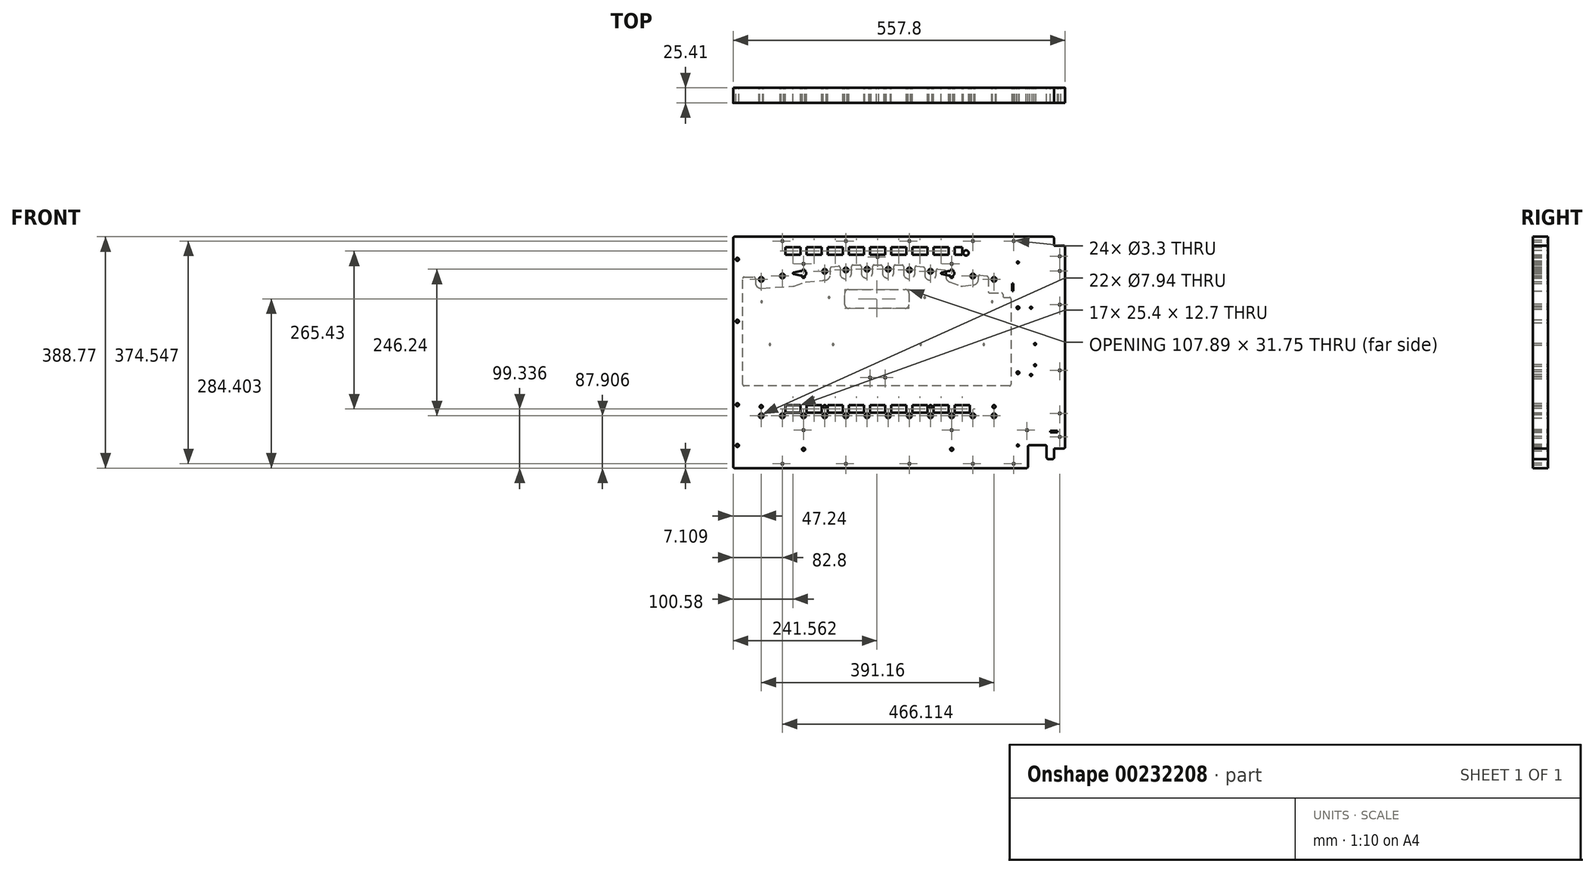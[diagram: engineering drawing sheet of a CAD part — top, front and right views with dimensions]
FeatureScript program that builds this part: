
annotation { "Feature Type Name" : "Feature", "Feature Type Description" : "" }
export const myFeature = defineFeature(function(context is Context, id is Id, definition is map)
    precondition{}
    {
        {
            var Q0;
            Q0=qCreatedBy(makeId("Front.planeOp"),FACE);
            var sketch = newSketch(context, id + "F0", { "sketchPlane" : qUnion([Q0])});
            skCircle(sketch, "E0", {"center": v(270.01, 168.97) * mm, "radius": 1.65 * mm});
            skCircle(sketch, "E1", {"center": v(270.01, 144.35) * mm, "radius": 1.65 * mm});
            skCircle(sketch, "E2", {"center": v(270.01, 87.69) * mm, "radius": 1.65 * mm});
            skCircle(sketch, "E3", {"center": v(270.01, -22.8) * mm, "radius": 1.65 * mm});
            skCircle(sketch, "E4", {"center": v(270.01, -134.56) * mm, "radius": 1.65 * mm});
            skCircle(sketch, "E5", {"center": v(270.01, -95.2) * mm, "radius": 1.65 * mm});
            skCircle(sketch, "E6", {"center": v(-196.1, -179.8) * mm, "radius": 1.65 * mm});
            skCircle(sketch, "E7", {"center": v(-89.42, -179.8) * mm, "radius": 1.65 * mm});
            skCircle(sketch, "E8", {"center": v(17.26, -179.8) * mm, "radius": 1.65 * mm});
            skCircle(sketch, "E9", {"center": v(123.94, -179.8) * mm, "radius": 1.65 * mm});
            skCircle(sketch, "E10", {"center": v(192.52, -179.8) * mm, "radius": 1.65 * mm});
            skCircle(sketch, "E11", {"center": v(-196.1, 194.75) * mm, "radius": 1.65 * mm});
            skCircle(sketch, "E12", {"center": v(-89.42, 194.75) * mm, "radius": 1.65 * mm});
            skCircle(sketch, "E13", {"center": v(17.26, 194.75) * mm, "radius": 1.65 * mm});
            skCircle(sketch, "E14", {"center": v(123.94, 194.75) * mm, "radius": 1.65 * mm});
            skCircle(sketch, "E15", {"center": v(192.52, 194.75) * mm, "radius": 1.65 * mm});
            skCircle(sketch, "E16", {"center": v(-196.1, 136) * mm, "radius": 3.97 * mm});
            skCircle(sketch, "E17", {"center": v(-124.98, 143.87) * mm, "radius": 3.97 * mm});
            skCircle(sketch, "E18", {"center": v(-89.42, 146.12) * mm, "radius": 3.97 * mm});
            skCircle(sketch, "E19", {"center": v(-53.86, 147.24) * mm, "radius": 3.97 * mm});
            skCircle(sketch, "E20", {"center": v(17.26, 146.12) * mm, "radius": 3.97 * mm});
            skCircle(sketch, "E21", {"center": v(-18.3, 147.24) * mm, "radius": 3.97 * mm});
            skCircle(sketch, "E22", {"center": v(52.82, 143.87) * mm, "radius": 3.97 * mm});
            skCircle(sketch, "E23", {"center": v(123.94, 136) * mm, "radius": 3.97 * mm});
            skCircle(sketch, "E24", {"center": v(-196.1, -99) * mm, "radius": 3.97 * mm});
            skCircle(sketch, "E25", {"center": v(-160.54, -99) * mm, "radius": 3.97 * mm});
            skCircle(sketch, "E26", {"center": v(-124.98, -99) * mm, "radius": 3.97 * mm});
            skCircle(sketch, "E27", {"center": v(-89.42, -99) * mm, "radius": 3.97 * mm});
            skCircle(sketch, "E28", {"center": v(-53.86, -99) * mm, "radius": 3.97 * mm});
            skCircle(sketch, "E29", {"center": v(-18.3, -99) * mm, "radius": 3.97 * mm});
            skCircle(sketch, "E30", {"center": v(17.26, -99) * mm, "radius": 3.97 * mm});
            skCircle(sketch, "E31", {"center": v(52.82, -99) * mm, "radius": 3.97 * mm});
            skCircle(sketch, "E32", {"center": v(88.38, -99) * mm, "radius": 3.97 * mm});
            skCircle(sketch, "E33", {"center": v(123.94, -99) * mm, "radius": 3.97 * mm});
            skCircle(sketch, "E34", {"center": v(159.5, 130.33) * mm, "radius": 3.97 * mm});
            skCircle(sketch, "E35", {"center": v(159.5, -99) * mm, "radius": 3.97 * mm});
            skCircle(sketch, "E36", {"center": v(-231.66, -99) * mm, "radius": 3.97 * mm});
            skCircle(sketch, "E37", {"center": v(-231.66, 130.33) * mm, "radius": 3.97 * mm});
            skCircle(sketch, "E38", {"center": v(-271.8, 163.89) * mm, "radius": 2.54 * mm});
            skCircle(sketch, "E39", {"center": v(-271.8, 59.75) * mm, "radius": 2.54 * mm});
            skCircle(sketch, "E40", {"center": v(-271.8, -148.94) * mm, "radius": 2.54 * mm});
            skCircle(sketch, "E41", {"center": v(-160.54, 156.27) * mm, "radius": 1.65 * mm});
            skCircle(sketch, "E42", {"center": v(88.38, 156.27) * mm, "radius": 1.65 * mm});
            skCircle(sketch, "E43", {"center": v(-36.08, 167.95) * mm, "radius": 1.65 * mm});
            skCircle(sketch, "E44", {"center": v(199.63, 82.6) * mm, "radius": 2.29 * mm});
            skCircle(sketch, "E45", {"center": v(221.73, 82.6) * mm, "radius": 1.66 * mm});
            skCircle(sketch, "E46", {"center": v(199.63, -26.61) * mm, "radius": 2.29 * mm});
            skCircle(sketch, "E47", {"center": v(221.73, -30.42) * mm, "radius": 1.66 * mm});
            skCircle(sketch, "E48", {"center": v(-160.54, -155.3) * mm, "radius": 2.54 * mm});
            skCircle(sketch, "E49", {"center": v(88.38, -155.3) * mm, "radius": 2.54 * mm});
            skCircle(sketch, "E50", {"center": v(-231.66, -83.76) * mm, "radius": 2.54 * mm});
            skCircle(sketch, "E51", {"center": v(159.5, -83.76) * mm, "radius": 2.54 * mm});
            skCircle(sketch, "E52", {"center": v(-160.54, -123.13) * mm, "radius": 1.65 * mm});
            skCircle(sketch, "E53", {"center": v(88.38, -123.13) * mm, "radius": 1.65 * mm});
            skCircle(sketch, "E54", {"center": v(-271.8, -80.36) * mm, "radius": 2.54 * mm});
            skCircle(sketch, "E55", {"center": v(-124.98, -83.76) * mm, "radius": 2.54 * mm});
            skCircle(sketch, "E56", {"center": v(52.82, -83.76) * mm, "radius": 2.54 * mm});
            skCircle(sketch, "E57", {"center": v(228.49, -13.91) * mm, "radius": 1.66 * mm});
            skCircle(sketch, "E58", {"center": v(228.49, 21.65) * mm, "radius": 1.66 * mm});
            skCircle(sketch, "E59", {"center": v(112.5, 174.6) * mm, "radius": 4.45 * mm});
            skCircle(sketch, "E60", {"center": v(199.63, 158.8) * mm, "radius": 1.66 * mm});
            skCircle(sketch, "E61", {"center": v(199.63, -148.94) * mm, "radius": 1.66 * mm});
            skCircle(sketch, "E62", {"center": v(-48.78, -34.87) * mm, "radius": 1.65 * mm});
            skCircle(sketch, "E63", {"center": v(-23.38, -34.87) * mm, "radius": 1.65 * mm});
            skCircle(sketch, "E64", {"center": v(214.97, -123.13) * mm, "radius": 1.65 * mm});
            skLineSegment(sketch, "E65", {"start": v(-48.78, 171.5) * mm, "end": v(-23.38, 171.5) * mm});
            skLineSegment(sketch, "E66", {"start": v(-23.38, 171.5) * mm, "end": v(-23.38, 184.2) * mm});
            skLineSegment(sketch, "E67", {"start": v(-23.38, 184.2) * mm, "end": v(-48.78, 184.2) * mm});
            skLineSegment(sketch, "E68", {"start": v(-48.78, 184.2) * mm, "end": v(-48.78, 171.5) * mm});
            skLineSegment(sketch, "E69", {"start": v(-58.94, 184.2) * mm, "end": v(-84.34, 184.2) * mm});
            skLineSegment(sketch, "E70", {"start": v(-84.34, 184.2) * mm, "end": v(-84.34, 171.5) * mm});
            skLineSegment(sketch, "E71", {"start": v(-84.34, 171.5) * mm, "end": v(-58.94, 171.5) * mm});
            skLineSegment(sketch, "E72", {"start": v(-58.94, 171.5) * mm, "end": v(-58.94, 184.2) * mm});
            skLineSegment(sketch, "E73", {"start": v(-94.5, 184.2) * mm, "end": v(-119.9, 184.2) * mm});
            skLineSegment(sketch, "E74", {"start": v(-119.9, 184.2) * mm, "end": v(-119.9, 171.5) * mm});
            skLineSegment(sketch, "E75", {"start": v(-119.9, 171.5) * mm, "end": v(-94.5, 171.5) * mm});
            skLineSegment(sketch, "E76", {"start": v(-94.5, 171.5) * mm, "end": v(-94.5, 184.2) * mm});
            skLineSegment(sketch, "E77", {"start": v(-130.06, 184.2) * mm, "end": v(-155.46, 184.2) * mm});
            skLineSegment(sketch, "E78", {"start": v(-155.46, 184.2) * mm, "end": v(-155.46, 171.5) * mm});
            skLineSegment(sketch, "E79", {"start": v(-155.46, 171.5) * mm, "end": v(-130.06, 171.5) * mm});
            skLineSegment(sketch, "E80", {"start": v(-130.06, 171.5) * mm, "end": v(-130.06, 184.2) * mm});
            skLineSegment(sketch, "E81", {"start": v(-165.62, 184.2) * mm, "end": v(-191.02, 184.2) * mm});
            skLineSegment(sketch, "E82", {"start": v(-191.02, 184.2) * mm, "end": v(-191.02, 171.5) * mm});
            skLineSegment(sketch, "E83", {"start": v(-191.02, 171.5) * mm, "end": v(-165.62, 171.5) * mm});
            skLineSegment(sketch, "E84", {"start": v(-165.62, 171.5) * mm, "end": v(-165.62, 184.2) * mm});
            skLineSegment(sketch, "E85", {"start": v(-13.22, 171.5) * mm, "end": v(12.18, 171.5) * mm});
            skLineSegment(sketch, "E86", {"start": v(12.18, 171.5) * mm, "end": v(12.18, 184.2) * mm});
            skLineSegment(sketch, "E87", {"start": v(12.18, 184.2) * mm, "end": v(-13.22, 184.2) * mm});
            skLineSegment(sketch, "E88", {"start": v(-13.22, 184.2) * mm, "end": v(-13.22, 171.5) * mm});
            skLineSegment(sketch, "E89", {"start": v(22.34, 171.5) * mm, "end": v(47.74, 171.5) * mm});
            skLineSegment(sketch, "E90", {"start": v(47.74, 171.5) * mm, "end": v(47.74, 184.2) * mm});
            skLineSegment(sketch, "E91", {"start": v(47.74, 184.2) * mm, "end": v(22.34, 184.2) * mm});
            skLineSegment(sketch, "E92", {"start": v(22.34, 184.2) * mm, "end": v(22.34, 171.5) * mm});
            skLineSegment(sketch, "E93", {"start": v(57.9, 171.5) * mm, "end": v(83.3, 171.5) * mm});
            skLineSegment(sketch, "E94", {"start": v(83.3, 171.5) * mm, "end": v(83.3, 184.2) * mm});
            skLineSegment(sketch, "E95", {"start": v(83.3, 184.2) * mm, "end": v(57.9, 184.2) * mm});
            skLineSegment(sketch, "E96", {"start": v(57.9, 184.2) * mm, "end": v(57.9, 171.5) * mm});
            skLineSegment(sketch, "E97", {"start": v(93.46, 171.5) * mm, "end": v(106.16, 171.5) * mm});
            skLineSegment(sketch, "E98", {"start": v(106.16, 171.5) * mm, "end": v(106.16, 184.2) * mm});
            skLineSegment(sketch, "E99", {"start": v(106.16, 184.2) * mm, "end": v(93.46, 184.2) * mm});
            skLineSegment(sketch, "E100", {"start": v(93.46, 184.2) * mm, "end": v(93.46, 171.5) * mm});
            skLineSegment(sketch, "E101", {"start": v(-48.78, -93.92) * mm, "end": v(-23.38, -93.92) * mm});
            skLineSegment(sketch, "E102", {"start": v(-23.38, -93.92) * mm, "end": v(-23.38, -81.22) * mm});
            skLineSegment(sketch, "E103", {"start": v(-23.38, -81.22) * mm, "end": v(-48.78, -81.22) * mm});
            skLineSegment(sketch, "E104", {"start": v(-48.78, -81.22) * mm, "end": v(-48.78, -93.92) * mm});
            skLineSegment(sketch, "E105", {"start": v(-58.94, -81.22) * mm, "end": v(-84.34, -81.22) * mm});
            skLineSegment(sketch, "E106", {"start": v(-84.34, -81.22) * mm, "end": v(-84.34, -93.92) * mm});
            skLineSegment(sketch, "E107", {"start": v(-84.34, -93.92) * mm, "end": v(-58.94, -93.92) * mm});
            skLineSegment(sketch, "E108", {"start": v(-58.94, -93.92) * mm, "end": v(-58.94, -81.22) * mm});
            skLineSegment(sketch, "E109", {"start": v(-94.5, -81.22) * mm, "end": v(-119.9, -81.22) * mm});
            skLineSegment(sketch, "E110", {"start": v(-119.9, -81.22) * mm, "end": v(-119.9, -93.92) * mm});
            skLineSegment(sketch, "E111", {"start": v(-119.9, -93.92) * mm, "end": v(-94.5, -93.92) * mm});
            skLineSegment(sketch, "E112", {"start": v(-94.5, -93.92) * mm, "end": v(-94.5, -81.22) * mm});
            skLineSegment(sketch, "E113", {"start": v(-130.06, -81.22) * mm, "end": v(-155.46, -81.22) * mm});
            skLineSegment(sketch, "E114", {"start": v(-155.46, -81.22) * mm, "end": v(-155.46, -93.92) * mm});
            skLineSegment(sketch, "E115", {"start": v(-155.46, -93.92) * mm, "end": v(-130.06, -93.92) * mm});
            skLineSegment(sketch, "E116", {"start": v(-130.06, -93.92) * mm, "end": v(-130.06, -81.22) * mm});
            skLineSegment(sketch, "E117", {"start": v(-165.62, -81.22) * mm, "end": v(-191.02, -81.22) * mm});
            skLineSegment(sketch, "E118", {"start": v(-191.02, -81.22) * mm, "end": v(-191.02, -93.92) * mm});
            skLineSegment(sketch, "E119", {"start": v(-191.02, -93.92) * mm, "end": v(-165.62, -93.92) * mm});
            skLineSegment(sketch, "E120", {"start": v(-165.62, -93.92) * mm, "end": v(-165.62, -81.22) * mm});
            skLineSegment(sketch, "E121", {"start": v(-13.22, -93.92) * mm, "end": v(12.18, -93.92) * mm});
            skLineSegment(sketch, "E122", {"start": v(12.18, -93.92) * mm, "end": v(12.18, -81.22) * mm});
            skLineSegment(sketch, "E123", {"start": v(12.18, -81.22) * mm, "end": v(-13.22, -81.22) * mm});
            skLineSegment(sketch, "E124", {"start": v(-13.22, -81.22) * mm, "end": v(-13.22, -93.92) * mm});
            skLineSegment(sketch, "E125", {"start": v(22.34, -93.92) * mm, "end": v(47.74, -93.92) * mm});
            skLineSegment(sketch, "E126", {"start": v(47.74, -93.92) * mm, "end": v(47.74, -81.22) * mm});
            skLineSegment(sketch, "E127", {"start": v(47.74, -81.22) * mm, "end": v(22.34, -81.22) * mm});
            skLineSegment(sketch, "E128", {"start": v(22.34, -81.22) * mm, "end": v(22.34, -93.92) * mm});
            skLineSegment(sketch, "E129", {"start": v(57.9, -93.92) * mm, "end": v(83.3, -93.92) * mm});
            skLineSegment(sketch, "E130", {"start": v(83.3, -93.92) * mm, "end": v(83.3, -81.22) * mm});
            skLineSegment(sketch, "E131", {"start": v(83.3, -81.22) * mm, "end": v(57.9, -81.22) * mm});
            skLineSegment(sketch, "E132", {"start": v(57.9, -81.22) * mm, "end": v(57.9, -93.92) * mm});
            skLineSegment(sketch, "E133", {"start": v(93.46, -93.92) * mm, "end": v(118.86, -93.92) * mm});
            skLineSegment(sketch, "E134", {"start": v(118.86, -93.92) * mm, "end": v(118.86, -81.22) * mm});
            skLineSegment(sketch, "E135", {"start": v(118.86, -81.22) * mm, "end": v(93.46, -81.22) * mm});
            skLineSegment(sketch, "E136", {"start": v(93.46, -81.22) * mm, "end": v(93.46, -93.92) * mm});
            skLineSegment(sketch, "E137", {"start": v(-163.33, 145.92) * mm, "end": v(-163.33, 144.06) * mm});
            skLineSegment(sketch, "E138", {"start": v(-163.33, 144.06) * mm, "end": v(-165.62, 144.06) * mm});
            skLineSegment(sketch, "E139", {"start": v(-165.62, 144.06) * mm, "end": v(-177.3, 141.75) * mm});
            skLineSegment(sketch, "E140", {"start": v(-177.3, 139.26) * mm, "end": v(-165.62, 136.95) * mm});
            skLineSegment(sketch, "E141", {"start": v(-165.62, 136.95) * mm, "end": v(-163.2, 136.95) * mm});
            skLineSegment(sketch, "E142", {"start": v(-162.32, 136.43) * mm, "end": v(-162.32, 133.1) * mm});
            skLineSegment(sketch, "E143", {"start": v(-158.76, 133.1) * mm, "end": v(-158.76, 136.43) * mm});
            skLineSegment(sketch, "E144", {"start": v(-157.75, 143.96) * mm, "end": v(-157.75, 145.92) * mm});
            skLineSegment(sketch, "E145", {"start": v(85.59, 145.92) * mm, "end": v(85.59, 144.06) * mm});
            skLineSegment(sketch, "E146", {"start": v(85.59, 144.06) * mm, "end": v(83.3, 144.06) * mm});
            skLineSegment(sketch, "E147", {"start": v(83.3, 144.06) * mm, "end": v(71.62, 141.75) * mm});
            skLineSegment(sketch, "E148", {"start": v(71.62, 139.26) * mm, "end": v(83.3, 136.95) * mm});
            skLineSegment(sketch, "E149", {"start": v(83.3, 136.95) * mm, "end": v(85.71, 136.95) * mm});
            skLineSegment(sketch, "E150", {"start": v(86.6, 136.43) * mm, "end": v(86.6, 133.1) * mm});
            skLineSegment(sketch, "E151", {"start": v(90.16, 133.1) * mm, "end": v(90.16, 136.43) * mm});
            skLineSegment(sketch, "E152", {"start": v(91.17, 143.96) * mm, "end": v(91.17, 145.92) * mm});
            skLineSegment(sketch, "E153", {"start": v(189.95, 110.55) * mm, "end": v(191.63, 110.55) * mm});
            skLineSegment(sketch, "E154", {"start": v(191.63, 110.55) * mm, "end": v(191.63, 123.25) * mm});
            skLineSegment(sketch, "E155", {"start": v(191.63, 123.25) * mm, "end": v(189.95, 123.25) * mm});
            skLineSegment(sketch, "E156", {"start": v(189.95, 123.25) * mm, "end": v(189.95, 110.55) * mm});
            skLineSegment(sketch, "E157", {"start": v(253.89, -124.4) * mm, "end": v(253.89, -126.94) * mm});
            skLineSegment(sketch, "E158", {"start": v(253.89, -126.94) * mm, "end": v(266.2, -126.94) * mm});
            skLineSegment(sketch, "E159", {"start": v(266.2, -126.94) * mm, "end": v(266.2, -124.4) * mm});
            skLineSegment(sketch, "E160", {"start": v(266.2, -124.4) * mm, "end": v(253.89, -124.4) * mm});
            skLineSegment(sketch, "E161", {"start": v(278.9, -151.48) * mm, "end": v(278.9, 184.2) * mm});
            skLineSegment(sketch, "E162", {"start": v(260.24, -154.02) * mm, "end": v(276.36, -154.02) * mm});
            skLineSegment(sketch, "E163", {"start": v(260.24, -169.26) * mm, "end": v(260.24, -154.02) * mm});
            skLineSegment(sketch, "E164", {"start": v(250.58, -171.8) * mm, "end": v(257.7, -171.8) * mm});
            skLineSegment(sketch, "E165", {"start": v(248.04, -150.97) * mm, "end": v(248.04, -169.26) * mm});
            skLineSegment(sketch, "E166", {"start": v(219.09, -148.43) * mm, "end": v(245.5, -148.43) * mm});
            skLineSegment(sketch, "E167", {"start": v(216.55, -184.37) * mm, "end": v(216.55, -150.97) * mm});
            skLineSegment(sketch, "E168", {"start": v(-276.36, -186.91) * mm, "end": v(214, -186.91) * mm});
            skLineSegment(sketch, "E169", {"start": v(-278.9, 199.32) * mm, "end": v(-278.9, -184.37) * mm});
            skLineSegment(sketch, "E170", {"start": v(257.7, 201.86) * mm, "end": v(-276.36, 201.86) * mm});
            skLineSegment(sketch, "E171", {"start": v(260.24, 186.75) * mm, "end": v(260.24, 199.32) * mm});
            skLineSegment(sketch, "E172", {"start": v(276.36, 186.75) * mm, "end": v(260.24, 186.75) * mm});
            skArc(sketch, "E173", {"start": v(-177.3, 141.75) * mm, "mid": v(-178.32, 140.5) * mm, "end": v(-177.3, 139.26) * mm});
            skArc(sketch, "E174", {"start": v(-163.2, 136.95) * mm, "mid": v(-162.78, 136.66) * mm, "end": v(-162.32, 136.43) * mm});
            skArc(sketch, "E175", {"start": v(-162.32, 133.1) * mm, "mid": v(-160.54, 132.88) * mm, "end": v(-158.76, 133.1) * mm});
            skArc(sketch, "E176", {"start": v(-158.76, 136.43) * mm, "mid": v(-156.14, 139.9) * mm, "end": v(-157.75, 143.96) * mm});
            skArc(sketch, "E177", {"start": v(-157.75, 145.92) * mm, "mid": v(-160.54, 146.6) * mm, "end": v(-163.33, 145.92) * mm});
            skArc(sketch, "E178", {"start": v(71.62, 141.75) * mm, "mid": v(70.6, 140.5) * mm, "end": v(71.62, 139.26) * mm});
            skArc(sketch, "E179", {"start": v(85.71, 136.95) * mm, "mid": v(86.14, 136.66) * mm, "end": v(86.6, 136.43) * mm});
            skArc(sketch, "E180", {"start": v(86.6, 133.1) * mm, "mid": v(88.38, 132.88) * mm, "end": v(90.16, 133.1) * mm});
            skArc(sketch, "E181", {"start": v(90.16, 136.43) * mm, "mid": v(92.78, 139.9) * mm, "end": v(91.17, 143.96) * mm});
            skArc(sketch, "E182", {"start": v(91.17, 145.92) * mm, "mid": v(88.38, 146.6) * mm, "end": v(85.59, 145.92) * mm});
            skArc(sketch, "E183", {"start": v(276.36, -154.02) * mm, "mid": v(278.16, -153.28) * mm, "end": v(278.9, -151.48) * mm});
            skArc(sketch, "E184", {"start": v(257.7, -171.8) * mm, "mid": v(259.5, -171.06) * mm, "end": v(260.24, -169.26) * mm});
            skArc(sketch, "E185", {"start": v(248.04, -169.26) * mm, "mid": v(248.79, -171.06) * mm, "end": v(250.58, -171.8) * mm});
            skArc(sketch, "E186", {"start": v(248.04, -150.97) * mm, "mid": v(247.3, -149.18) * mm, "end": v(245.5, -148.43) * mm});
            skArc(sketch, "E187", {"start": v(219.09, -148.43) * mm, "mid": v(217.3, -149.18) * mm, "end": v(216.55, -150.97) * mm});
            skArc(sketch, "E188", {"start": v(214, -186.91) * mm, "mid": v(215.8, -186.17) * mm, "end": v(216.55, -184.37) * mm});
            skArc(sketch, "E189", {"start": v(-278.9, -184.37) * mm, "mid": v(-278.16, -186.17) * mm, "end": v(-276.36, -186.91) * mm});
            skArc(sketch, "E190", {"start": v(-276.36, 201.86) * mm, "mid": v(-278.16, 201.11) * mm, "end": v(-278.9, 199.32) * mm});
            skArc(sketch, "E191", {"start": v(260.24, 199.32) * mm, "mid": v(259.5, 201.11) * mm, "end": v(257.7, 201.86) * mm});
            skArc(sketch, "E192", {"start": v(278.9, 184.2) * mm, "mid": v(278.16, 186) * mm, "end": v(276.36, 186.75) * mm});
            skSolve(sketch);
        }
        {
            var Q0;
            Q0 = qSketchRegion(id + "F0", true);
            extrude(context, id + "F1", {"entities" : qUnion([Q0]), "depth" : 25.4 * mm});
        }
        {
            var Q0;
            Q0=makeQuery(id+"F1.opExtrude","CAP_FACE",FACE,{"disambiguationData":[OSD([sQuery(id+"F0.wireOp",EDGE,"E0"),sQuery(id+"F0.wireOp",EDGE,"E1"),sQuery(id+"F0.wireOp",EDGE,"E2"),sQuery(id+"F0.wireOp",EDGE,"E3"),sQuery(id+"F0.wireOp",EDGE,"E4"),sQuery(id+"F0.wireOp",EDGE,"E5"),sQuery(id+"F0.wireOp",EDGE,"E6"),sQuery(id+"F0.wireOp",EDGE,"E7"),sQuery(id+"F0.wireOp",EDGE,"E8"),sQuery(id+"F0.wireOp",EDGE,"E9"),sQuery(id+"F0.wireOp",EDGE,"E10"),sQuery(id+"F0.wireOp",EDGE,"E11"),sQuery(id+"F0.wireOp",EDGE,"E12"),sQuery(id+"F0.wireOp",EDGE,"E13"),sQuery(id+"F0.wireOp",EDGE,"E14"),sQuery(id+"F0.wireOp",EDGE,"E15"),sQuery(id+"F0.wireOp",EDGE,"E16"),sQuery(id+"F0.wireOp",EDGE,"E17"),sQuery(id+"F0.wireOp",EDGE,"E18"),sQuery(id+"F0.wireOp",EDGE,"E19"),sQuery(id+"F0.wireOp",EDGE,"E20"),sQuery(id+"F0.wireOp",EDGE,"E21"),sQuery(id+"F0.wireOp",EDGE,"E22"),sQuery(id+"F0.wireOp",EDGE,"E23"),sQuery(id+"F0.wireOp",EDGE,"E24"),sQuery(id+"F0.wireOp",EDGE,"E25"),sQuery(id+"F0.wireOp",EDGE,"E26"),sQuery(id+"F0.wireOp",EDGE,"E27"),sQuery(id+"F0.wireOp",EDGE,"E28"),sQuery(id+"F0.wireOp",EDGE,"E29"),sQuery(id+"F0.wireOp",EDGE,"E30"),sQuery(id+"F0.wireOp",EDGE,"E31"),sQuery(id+"F0.wireOp",EDGE,"E32"),sQuery(id+"F0.wireOp",EDGE,"E33"),sQuery(id+"F0.wireOp",EDGE,"E34"),sQuery(id+"F0.wireOp",EDGE,"E35"),sQuery(id+"F0.wireOp",EDGE,"E36"),sQuery(id+"F0.wireOp",EDGE,"E37"),sQuery(id+"F0.wireOp",EDGE,"E38"),sQuery(id+"F0.wireOp",EDGE,"E39"),sQuery(id+"F0.wireOp",EDGE,"E40"),sQuery(id+"F0.wireOp",EDGE,"E41"),sQuery(id+"F0.wireOp",EDGE,"E42"),sQuery(id+"F0.wireOp",EDGE,"E43"),sQuery(id+"F0.wireOp",EDGE,"E44"),sQuery(id+"F0.wireOp",EDGE,"E45"),sQuery(id+"F0.wireOp",EDGE,"E46"),sQuery(id+"F0.wireOp",EDGE,"E47"),sQuery(id+"F0.wireOp",EDGE,"E48"),sQuery(id+"F0.wireOp",EDGE,"E49"),sQuery(id+"F0.wireOp",EDGE,"E50"),sQuery(id+"F0.wireOp",EDGE,"E51"),sQuery(id+"F0.wireOp",EDGE,"E52"),sQuery(id+"F0.wireOp",EDGE,"E53"),sQuery(id+"F0.wireOp",EDGE,"E54"),sQuery(id+"F0.wireOp",EDGE,"E55"),sQuery(id+"F0.wireOp",EDGE,"E56"),sQuery(id+"F0.wireOp",EDGE,"E57"),sQuery(id+"F0.wireOp",EDGE,"E58"),sQuery(id+"F0.wireOp",EDGE,"E59"),sQuery(id+"F0.wireOp",EDGE,"E60"),sQuery(id+"F0.wireOp",EDGE,"E61"),sQuery(id+"F0.wireOp",EDGE,"E62"),sQuery(id+"F0.wireOp",EDGE,"E63"),sQuery(id+"F0.wireOp",EDGE,"E64"),sQuery(id+"F0.wireOp",EDGE,"E65"),sQuery(id+"F0.wireOp",EDGE,"E66"),sQuery(id+"F0.wireOp",EDGE,"E67"),sQuery(id+"F0.wireOp",EDGE,"E68"),sQuery(id+"F0.wireOp",EDGE,"E69"),sQuery(id+"F0.wireOp",EDGE,"E70"),sQuery(id+"F0.wireOp",EDGE,"E71"),sQuery(id+"F0.wireOp",EDGE,"E72"),sQuery(id+"F0.wireOp",EDGE,"E73"),sQuery(id+"F0.wireOp",EDGE,"E74"),sQuery(id+"F0.wireOp",EDGE,"E75"),sQuery(id+"F0.wireOp",EDGE,"E76"),sQuery(id+"F0.wireOp",EDGE,"E77"),sQuery(id+"F0.wireOp",EDGE,"E78"),sQuery(id+"F0.wireOp",EDGE,"E79"),sQuery(id+"F0.wireOp",EDGE,"E80"),sQuery(id+"F0.wireOp",EDGE,"E81"),sQuery(id+"F0.wireOp",EDGE,"E82"),sQuery(id+"F0.wireOp",EDGE,"E83"),sQuery(id+"F0.wireOp",EDGE,"E84"),sQuery(id+"F0.wireOp",EDGE,"E85"),sQuery(id+"F0.wireOp",EDGE,"E86"),sQuery(id+"F0.wireOp",EDGE,"E87"),sQuery(id+"F0.wireOp",EDGE,"E88"),sQuery(id+"F0.wireOp",EDGE,"E89"),sQuery(id+"F0.wireOp",EDGE,"E90"),sQuery(id+"F0.wireOp",EDGE,"E91"),sQuery(id+"F0.wireOp",EDGE,"E92"),sQuery(id+"F0.wireOp",EDGE,"E93"),sQuery(id+"F0.wireOp",EDGE,"E94"),sQuery(id+"F0.wireOp",EDGE,"E95"),sQuery(id+"F0.wireOp",EDGE,"E96"),sQuery(id+"F0.wireOp",EDGE,"E97"),sQuery(id+"F0.wireOp",EDGE,"E98"),sQuery(id+"F0.wireOp",EDGE,"E99"),sQuery(id+"F0.wireOp",EDGE,"E100"),sQuery(id+"F0.wireOp",EDGE,"E101"),sQuery(id+"F0.wireOp",EDGE,"E102"),sQuery(id+"F0.wireOp",EDGE,"E103"),sQuery(id+"F0.wireOp",EDGE,"E104"),sQuery(id+"F0.wireOp",EDGE,"E105"),sQuery(id+"F0.wireOp",EDGE,"E106"),sQuery(id+"F0.wireOp",EDGE,"E107"),sQuery(id+"F0.wireOp",EDGE,"E108"),sQuery(id+"F0.wireOp",EDGE,"E109"),sQuery(id+"F0.wireOp",EDGE,"E110"),sQuery(id+"F0.wireOp",EDGE,"E111"),sQuery(id+"F0.wireOp",EDGE,"E112"),sQuery(id+"F0.wireOp",EDGE,"E113"),sQuery(id+"F0.wireOp",EDGE,"E114"),sQuery(id+"F0.wireOp",EDGE,"E115"),sQuery(id+"F0.wireOp",EDGE,"E116"),sQuery(id+"F0.wireOp",EDGE,"E117"),sQuery(id+"F0.wireOp",EDGE,"E118"),sQuery(id+"F0.wireOp",EDGE,"E119"),sQuery(id+"F0.wireOp",EDGE,"E120"),sQuery(id+"F0.wireOp",EDGE,"E121"),sQuery(id+"F0.wireOp",EDGE,"E122"),sQuery(id+"F0.wireOp",EDGE,"E123"),sQuery(id+"F0.wireOp",EDGE,"E124"),sQuery(id+"F0.wireOp",EDGE,"E125"),sQuery(id+"F0.wireOp",EDGE,"E126"),sQuery(id+"F0.wireOp",EDGE,"E127"),sQuery(id+"F0.wireOp",EDGE,"E128"),sQuery(id+"F0.wireOp",EDGE,"E129"),sQuery(id+"F0.wireOp",EDGE,"E130"),sQuery(id+"F0.wireOp",EDGE,"E131"),sQuery(id+"F0.wireOp",EDGE,"E132"),sQuery(id+"F0.wireOp",EDGE,"E133"),sQuery(id+"F0.wireOp",EDGE,"E134"),sQuery(id+"F0.wireOp",EDGE,"E135"),sQuery(id+"F0.wireOp",EDGE,"E136"),sQuery(id+"F0.wireOp",EDGE,"E137"),sQuery(id+"F0.wireOp",EDGE,"E138"),sQuery(id+"F0.wireOp",EDGE,"E139"),sQuery(id+"F0.wireOp",EDGE,"E140"),sQuery(id+"F0.wireOp",EDGE,"E141"),sQuery(id+"F0.wireOp",EDGE,"E142"),sQuery(id+"F0.wireOp",EDGE,"E143"),sQuery(id+"F0.wireOp",EDGE,"E144"),sQuery(id+"F0.wireOp",EDGE,"E145"),sQuery(id+"F0.wireOp",EDGE,"E146"),sQuery(id+"F0.wireOp",EDGE,"E147"),sQuery(id+"F0.wireOp",EDGE,"E148"),sQuery(id+"F0.wireOp",EDGE,"E149"),sQuery(id+"F0.wireOp",EDGE,"E150"),sQuery(id+"F0.wireOp",EDGE,"E151"),sQuery(id+"F0.wireOp",EDGE,"E152"),sQuery(id+"F0.wireOp",EDGE,"E153"),sQuery(id+"F0.wireOp",EDGE,"E154"),sQuery(id+"F0.wireOp",EDGE,"E155"),sQuery(id+"F0.wireOp",EDGE,"E156"),sQuery(id+"F0.wireOp",EDGE,"E157"),sQuery(id+"F0.wireOp",EDGE,"E158"),sQuery(id+"F0.wireOp",EDGE,"E159"),sQuery(id+"F0.wireOp",EDGE,"E160"),sQuery(id+"F0.wireOp",EDGE,"E161"),sQuery(id+"F0.wireOp",EDGE,"E162"),sQuery(id+"F0.wireOp",EDGE,"E163"),sQuery(id+"F0.wireOp",EDGE,"E164"),sQuery(id+"F0.wireOp",EDGE,"E165"),sQuery(id+"F0.wireOp",EDGE,"E166"),sQuery(id+"F0.wireOp",EDGE,"E167"),sQuery(id+"F0.wireOp",EDGE,"E168"),sQuery(id+"F0.wireOp",EDGE,"E169"),sQuery(id+"F0.wireOp",EDGE,"E170"),sQuery(id+"F0.wireOp",EDGE,"E171"),sQuery(id+"F0.wireOp",EDGE,"E172"),sQuery(id+"F0.wireOp",EDGE,"E173"),sQuery(id+"F0.wireOp",EDGE,"E174"),sQuery(id+"F0.wireOp",EDGE,"E175"),sQuery(id+"F0.wireOp",EDGE,"E176"),sQuery(id+"F0.wireOp",EDGE,"E177"),sQuery(id+"F0.wireOp",EDGE,"E178"),sQuery(id+"F0.wireOp",EDGE,"E179"),sQuery(id+"F0.wireOp",EDGE,"E180"),sQuery(id+"F0.wireOp",EDGE,"E181"),sQuery(id+"F0.wireOp",EDGE,"E182"),sQuery(id+"F0.wireOp",EDGE,"E183"),sQuery(id+"F0.wireOp",EDGE,"E184"),sQuery(id+"F0.wireOp",EDGE,"E185"),sQuery(id+"F0.wireOp",EDGE,"E186"),sQuery(id+"F0.wireOp",EDGE,"E187"),sQuery(id+"F0.wireOp",EDGE,"E188"),sQuery(id+"F0.wireOp",EDGE,"E189"),sQuery(id+"F0.wireOp",EDGE,"E190"),sQuery(id+"F0.wireOp",EDGE,"E191"),sQuery(id+"F0.wireOp",EDGE,"E192")])],"isStart":true});
            var sketch = newSketch(context, id + "F2", { "sketchPlane" : qUnion([Q0])});
            skCircle(sketch, "E193", {"center": v(179.69, -32.1) * mm, "radius": 1.46 * mm});
            skCircle(sketch, "E194", {"center": v(80.4, 47) * mm, "radius": 1.46 * mm});
            skCircle(sketch, "E195", {"center": v(-80.4, 47) * mm, "radius": 1.46 * mm});
            skCircle(sketch, "E196", {"center": v(-179.69, -32.1) * mm, "radius": 1.46 * mm});
            skLineSegment(sketch, "E197", {"start": v(-225.43, 44.45) * mm, "end": v(-225.43, -99.06) * mm});
            skArc(sketch, "E198", {"start": v(-225.43, -99.06) * mm, "mid": v(-224.68, -100.86) * mm, "end": v(-222.89, -101.6) * mm});
            skLineSegment(sketch, "E199", {"start": v(-222.89, -101.6) * mm, "end": v(222.88, -101.6) * mm});
            skArc(sketch, "E200", {"start": v(222.88, -101.6) * mm, "mid": v(224.68, -100.86) * mm, "end": v(225.42, -99.06) * mm});
            skLineSegment(sketch, "E201", {"start": v(225.43, -99.06) * mm, "end": v(225.43, 78.74) * mm});
            skArc(sketch, "E202", {"start": v(225.42, 78.74) * mm, "mid": v(224.68, 80.54) * mm, "end": v(222.88, 81.28) * mm});
            skLineSegment(sketch, "E203", {"start": v(222.88, 81.28) * mm, "end": v(206.63, 81.28) * mm});
            skArc(sketch, "E204", {"start": v(206.63, 81.28) * mm, "mid": v(204.83, 80.54) * mm, "end": v(204.09, 78.74) * mm});
            skLineSegment(sketch, "E205", {"start": v(204.09, 78.74) * mm, "end": v(204.09, 71.85) * mm});
            skArc(sketch, "E206", {"start": v(193.92, 62.35) * mm, "mid": v(201.07, 64.9) * mm, "end": v(204.09, 71.85) * mm});
            skLineSegment(sketch, "E207", {"start": v(193.92, 62.35) * mm, "end": v(140.8, 65.96) * mm});
            skArc(sketch, "E208", {"start": v(139.09, 66.32) * mm, "mid": v(139.93, 66.08) * mm, "end": v(140.8, 65.96) * mm});
            skLineSegment(sketch, "E209", {"start": v(139.09, 66.32) * mm, "end": v(120.24, 73.06) * mm});
            skArc(sketch, "E210", {"start": v(113.92, 82.03) * mm, "mid": v(115.66, 76.54) * mm, "end": v(120.24, 73.06) * mm});
            skLineSegment(sketch, "E211", {"start": v(113.92, 82.03) * mm, "end": v(113.92, 90.6) * mm});
            skArc(sketch, "E212", {"start": v(113.92, 90.6) * mm, "mid": v(113.3, 92.26) * mm, "end": v(111.74, 93.1) * mm});
            skLineSegment(sketch, "E213", {"start": v(111.74, 93.1) * mm, "end": v(100.3, 94.74) * mm});
            skArc(sketch, "E214", {"start": v(100.3, 94.74) * mm, "mid": v(98.28, 94.15) * mm, "end": v(97.4, 92.23) * mm});
            skLineSegment(sketch, "E215", {"start": v(97.4, 92.23) * mm, "end": v(97.4, 85.4) * mm});
            skArc(sketch, "E216", {"start": v(78.36, 85.4) * mm, "mid": v(87.88, 75.87) * mm, "end": v(97.4, 85.4) * mm});
            skLineSegment(sketch, "E217", {"start": v(78.36, 85.4) * mm, "end": v(78.36, 95.67) * mm});
            skArc(sketch, "E218", {"start": v(78.36, 95.67) * mm, "mid": v(77.74, 97.34) * mm, "end": v(76.18, 98.19) * mm});
            skLineSegment(sketch, "E219", {"start": v(76.18, 98.19) * mm, "end": v(64.75, 99.82) * mm});
            skArc(sketch, "E220", {"start": v(64.75, 99.82) * mm, "mid": v(62.72, 99.23) * mm, "end": v(61.85, 97.3) * mm});
            skLineSegment(sketch, "E221", {"start": v(61.85, 97.3) * mm, "end": v(61.85, 87.64) * mm});
            skArc(sketch, "E222", {"start": v(42.8, 87.64) * mm, "mid": v(52.32, 78.12) * mm, "end": v(61.85, 87.64) * mm});
            skLineSegment(sketch, "E223", {"start": v(42.8, 87.64) * mm, "end": v(42.8, 99.06) * mm});
            skArc(sketch, "E224", {"start": v(42.8, 99.06) * mm, "mid": v(42.06, 100.86) * mm, "end": v(40.26, 101.6) * mm});
            skLineSegment(sketch, "E225", {"start": v(40.26, 101.6) * mm, "end": v(28.83, 101.6) * mm});
            skArc(sketch, "E226", {"start": v(28.83, 101.6) * mm, "mid": v(27.03, 100.86) * mm, "end": v(26.29, 99.06) * mm});
            skLineSegment(sketch, "E227", {"start": v(26.29, 99.06) * mm, "end": v(26.29, 88.76) * mm});
            skArc(sketch, "E228", {"start": v(7.24, 88.76) * mm, "mid": v(16.76, 79.24) * mm, "end": v(26.29, 88.76) * mm});
            skLineSegment(sketch, "E229", {"start": v(7.24, 88.76) * mm, "end": v(7.24, 99.06) * mm});
            skArc(sketch, "E230", {"start": v(7.24, 99.06) * mm, "mid": v(6.5, 100.86) * mm, "end": v(4.7, 101.6) * mm});
            skLineSegment(sketch, "E231", {"start": v(4.7, 101.6) * mm, "end": v(-6.73, 101.6) * mm});
            skArc(sketch, "E232", {"start": v(-6.73, 101.6) * mm, "mid": v(-8.53, 100.86) * mm, "end": v(-9.27, 99.06) * mm});
            skLineSegment(sketch, "E233", {"start": v(-9.27, 99.06) * mm, "end": v(-9.27, 88.76) * mm});
            skArc(sketch, "E234", {"start": v(-28.32, 88.76) * mm, "mid": v(-18.8, 79.24) * mm, "end": v(-9.27, 88.76) * mm});
            skLineSegment(sketch, "E235", {"start": v(-28.32, 88.76) * mm, "end": v(-28.32, 99.06) * mm});
            skArc(sketch, "E236", {"start": v(-28.32, 99.06) * mm, "mid": v(-29.06, 100.86) * mm, "end": v(-30.86, 101.6) * mm});
            skLineSegment(sketch, "E237", {"start": v(-30.86, 101.6) * mm, "end": v(-42.3, 101.6) * mm});
            skArc(sketch, "E238", {"start": v(-42.3, 101.6) * mm, "mid": v(-44.09, 100.86) * mm, "end": v(-44.83, 99.06) * mm});
            skLineSegment(sketch, "E239", {"start": v(-44.83, 99.06) * mm, "end": v(-44.83, 87.64) * mm});
            skArc(sketch, "E240", {"start": v(-63.88, 87.64) * mm, "mid": v(-54.36, 78.12) * mm, "end": v(-44.83, 87.64) * mm});
            skLineSegment(sketch, "E241", {"start": v(-63.88, 87.64) * mm, "end": v(-63.88, 97.3) * mm});
            skArc(sketch, "E242", {"start": v(-63.88, 97.3) * mm, "mid": v(-64.76, 99.22) * mm, "end": v(-66.78, 99.82) * mm});
            skLineSegment(sketch, "E243", {"start": v(-66.78, 99.82) * mm, "end": v(-78.21, 98.19) * mm});
            skArc(sketch, "E244", {"start": v(-78.21, 98.19) * mm, "mid": v(-79.77, 97.34) * mm, "end": v(-80.4, 95.67) * mm});
            skLineSegment(sketch, "E245", {"start": v(-80.4, 95.67) * mm, "end": v(-80.4, 85.4) * mm});
            skArc(sketch, "E246", {"start": v(-99.44, 85.4) * mm, "mid": v(-89.92, 75.87) * mm, "end": v(-80.4, 85.4) * mm});
            skLineSegment(sketch, "E247", {"start": v(-99.44, 85.4) * mm, "end": v(-99.44, 92.22) * mm});
            skArc(sketch, "E248", {"start": v(-99.44, 92.22) * mm, "mid": v(-100.32, 94.14) * mm, "end": v(-102.34, 94.74) * mm});
            skLineSegment(sketch, "E249", {"start": v(-102.34, 94.74) * mm, "end": v(-113.77, 93.1) * mm});
            skArc(sketch, "E250", {"start": v(-113.77, 93.1) * mm, "mid": v(-115.33, 92.26) * mm, "end": v(-115.95, 90.6) * mm});
            skLineSegment(sketch, "E251", {"start": v(-115.95, 90.6) * mm, "end": v(-115.95, 82.03) * mm});
            skArc(sketch, "E252", {"start": v(-122.27, 73.06) * mm, "mid": v(-117.69, 76.54) * mm, "end": v(-115.95, 82.03) * mm});
            skLineSegment(sketch, "E253", {"start": v(-122.27, 73.06) * mm, "end": v(-141.12, 66.32) * mm});
            skArc(sketch, "E254", {"start": v(-143.97, 65.99) * mm, "mid": v(-142.53, 65.99) * mm, "end": v(-141.12, 66.32) * mm});
            skLineSegment(sketch, "E255", {"start": v(-143.97, 65.99) * mm, "end": v(-162.11, 68.05) * mm});
            skArc(sketch, "E256", {"start": v(-170.56, 77.52) * mm, "mid": v(-168.14, 71.17) * mm, "end": v(-162.11, 68.05) * mm});
            skLineSegment(sketch, "E257", {"start": v(-170.56, 77.52) * mm, "end": v(-170.56, 82.06) * mm});
            skArc(sketch, "E258", {"start": v(-170.56, 82.06) * mm, "mid": v(-171.44, 83.98) * mm, "end": v(-173.46, 84.58) * mm});
            skLineSegment(sketch, "E259", {"start": v(-173.46, 84.58) * mm, "end": v(-184.9, 82.94) * mm});
            skArc(sketch, "E260", {"start": v(-184.9, 82.94) * mm, "mid": v(-186.45, 82.1) * mm, "end": v(-187.07, 80.43) * mm});
            skLineSegment(sketch, "E261", {"start": v(-187.07, 80.43) * mm, "end": v(-187.07, 57.15) * mm});
            skArc(sketch, "E262", {"start": v(-189.61, 54.61) * mm, "mid": v(-187.81, 55.35) * mm, "end": v(-187.07, 57.15) * mm});
            skLineSegment(sketch, "E263", {"start": v(-189.61, 54.61) * mm, "end": v(-209.27, 54.61) * mm});
            skArc(sketch, "E264", {"start": v(-209.27, 54.6) * mm, "mid": v(-211.06, 53.87) * mm, "end": v(-211.8, 52.07) * mm});
            skLineSegment(sketch, "E265", {"start": v(-211.8, 52.07) * mm, "end": v(-211.8, 49.53) * mm});
            skArc(sketch, "E266", {"start": v(-214.35, 47) * mm, "mid": v(-212.55, 47.73) * mm, "end": v(-211.8, 49.53) * mm});
            skLineSegment(sketch, "E267", {"start": v(-214.35, 47) * mm, "end": v(-222.89, 47) * mm});
            skArc(sketch, "E268", {"start": v(-222.89, 47) * mm, "mid": v(-224.68, 46.25) * mm, "end": v(-225.43, 44.45) * mm});
            skLineSegment(sketch, "E269", {"start": v(-47.6, 28.79) * mm, "end": v(47.6, 28.79) * mm});
            skArc(sketch, "E270", {"start": v(-53.95, 35.14) * mm, "mid": v(-52.09, 30.65) * mm, "end": v(-47.6, 28.79) * mm});
            skLineSegment(sketch, "E271", {"start": v(-53.95, 54.19) * mm, "end": v(-53.95, 35.14) * mm});
            skArc(sketch, "E272", {"start": v(-47.6, 60.54) * mm, "mid": v(-52.09, 58.68) * mm, "end": v(-53.95, 54.19) * mm});
            skLineSegment(sketch, "E273", {"start": v(47.6, 60.54) * mm, "end": v(-47.6, 60.54) * mm});
            skArc(sketch, "E274", {"start": v(53.95, 54.19) * mm, "mid": v(52.09, 58.68) * mm, "end": v(47.6, 60.54) * mm});
            skLineSegment(sketch, "E275", {"start": v(53.95, 35.14) * mm, "end": v(53.95, 54.19) * mm});
            skArc(sketch, "E276", {"start": v(47.6, 28.79) * mm, "mid": v(52.09, 30.65) * mm, "end": v(53.95, 35.14) * mm});
            skCircle(sketch, "E277", {"center": v(-73.51, -32.1) * mm, "radius": 1.46 * mm});
            skCircle(sketch, "E278", {"center": v(-193.68, 39.86) * mm, "radius": 1.46 * mm});
            skCircle(sketch, "E279", {"center": v(193.68, 39.86) * mm, "radius": 1.46 * mm});
            skCircle(sketch, "E280", {"center": v(73.51, -32.1) * mm, "radius": 1.46 * mm});
            skSolve(sketch);
        }
        {
            var Q0;
            Q0=qSketchRegion(id+"F2",true);
            extrude(context, id + "F3", {"entities" : qUnion([Q0]), "depth" : 0.01 * mm});
        }
        {
            var Q0;
            Q0=makeQuery(id+"F3.opExtrude","CAP_FACE",FACE,{"disambiguationData":[OSD([sQuery(id+"F2.wireOp",EDGE,"E193"),sQuery(id+"F2.wireOp",EDGE,"E194"),sQuery(id+"F2.wireOp",EDGE,"E195"),sQuery(id+"F2.wireOp",EDGE,"E196"),sQuery(id+"F2.wireOp",EDGE,"E197"),sQuery(id+"F2.wireOp",EDGE,"E198"),sQuery(id+"F2.wireOp",EDGE,"E199"),sQuery(id+"F2.wireOp",EDGE,"E200"),sQuery(id+"F2.wireOp",EDGE,"E201"),sQuery(id+"F2.wireOp",EDGE,"E202"),sQuery(id+"F2.wireOp",EDGE,"E203"),sQuery(id+"F2.wireOp",EDGE,"E204"),sQuery(id+"F2.wireOp",EDGE,"E205"),sQuery(id+"F2.wireOp",EDGE,"E206"),sQuery(id+"F2.wireOp",EDGE,"E207"),sQuery(id+"F2.wireOp",EDGE,"E208"),sQuery(id+"F2.wireOp",EDGE,"E209"),sQuery(id+"F2.wireOp",EDGE,"E210"),sQuery(id+"F2.wireOp",EDGE,"E211"),sQuery(id+"F2.wireOp",EDGE,"E212"),sQuery(id+"F2.wireOp",EDGE,"E213"),sQuery(id+"F2.wireOp",EDGE,"E214"),sQuery(id+"F2.wireOp",EDGE,"E215"),sQuery(id+"F2.wireOp",EDGE,"E216"),sQuery(id+"F2.wireOp",EDGE,"E217"),sQuery(id+"F2.wireOp",EDGE,"E218"),sQuery(id+"F2.wireOp",EDGE,"E219"),sQuery(id+"F2.wireOp",EDGE,"E220"),sQuery(id+"F2.wireOp",EDGE,"E221"),sQuery(id+"F2.wireOp",EDGE,"E222"),sQuery(id+"F2.wireOp",EDGE,"E223"),sQuery(id+"F2.wireOp",EDGE,"E224"),sQuery(id+"F2.wireOp",EDGE,"E225"),sQuery(id+"F2.wireOp",EDGE,"E226"),sQuery(id+"F2.wireOp",EDGE,"E227"),sQuery(id+"F2.wireOp",EDGE,"E228"),sQuery(id+"F2.wireOp",EDGE,"E229"),sQuery(id+"F2.wireOp",EDGE,"E230"),sQuery(id+"F2.wireOp",EDGE,"E231"),sQuery(id+"F2.wireOp",EDGE,"E232"),sQuery(id+"F2.wireOp",EDGE,"E233"),sQuery(id+"F2.wireOp",EDGE,"E234"),sQuery(id+"F2.wireOp",EDGE,"E235"),sQuery(id+"F2.wireOp",EDGE,"E236"),sQuery(id+"F2.wireOp",EDGE,"E237"),sQuery(id+"F2.wireOp",EDGE,"E238"),sQuery(id+"F2.wireOp",EDGE,"E239"),sQuery(id+"F2.wireOp",EDGE,"E240"),sQuery(id+"F2.wireOp",EDGE,"E241"),sQuery(id+"F2.wireOp",EDGE,"E242"),sQuery(id+"F2.wireOp",EDGE,"E243"),sQuery(id+"F2.wireOp",EDGE,"E244"),sQuery(id+"F2.wireOp",EDGE,"E245"),sQuery(id+"F2.wireOp",EDGE,"E246"),sQuery(id+"F2.wireOp",EDGE,"E247"),sQuery(id+"F2.wireOp",EDGE,"E248"),sQuery(id+"F2.wireOp",EDGE,"E249"),sQuery(id+"F2.wireOp",EDGE,"E250"),sQuery(id+"F2.wireOp",EDGE,"E251"),sQuery(id+"F2.wireOp",EDGE,"E252"),sQuery(id+"F2.wireOp",EDGE,"E253"),sQuery(id+"F2.wireOp",EDGE,"E254"),sQuery(id+"F2.wireOp",EDGE,"E255"),sQuery(id+"F2.wireOp",EDGE,"E256"),sQuery(id+"F2.wireOp",EDGE,"E257"),sQuery(id+"F2.wireOp",EDGE,"E258"),sQuery(id+"F2.wireOp",EDGE,"E259"),sQuery(id+"F2.wireOp",EDGE,"E260"),sQuery(id+"F2.wireOp",EDGE,"E261"),sQuery(id+"F2.wireOp",EDGE,"E262"),sQuery(id+"F2.wireOp",EDGE,"E263"),sQuery(id+"F2.wireOp",EDGE,"E264"),sQuery(id+"F2.wireOp",EDGE,"E265"),sQuery(id+"F2.wireOp",EDGE,"E266"),sQuery(id+"F2.wireOp",EDGE,"E267"),sQuery(id+"F2.wireOp",EDGE,"E268"),sQuery(id+"F2.wireOp",EDGE,"E269"),sQuery(id+"F2.wireOp",EDGE,"E270"),sQuery(id+"F2.wireOp",EDGE,"E271"),sQuery(id+"F2.wireOp",EDGE,"E272"),sQuery(id+"F2.wireOp",EDGE,"E273"),sQuery(id+"F2.wireOp",EDGE,"E274"),sQuery(id+"F2.wireOp",EDGE,"E275"),sQuery(id+"F2.wireOp",EDGE,"E276"),sQuery(id+"F2.wireOp",EDGE,"E277"),sQuery(id+"F2.wireOp",EDGE,"E278"),sQuery(id+"F2.wireOp",EDGE,"E279"),sQuery(id+"F2.wireOp",EDGE,"E280")])],"isStart":false});
            var sketch = newSketch(context, id + "F4", { "sketchPlane" : qUnion([Q0])});
            skLineSegment(sketch, "E281", {"start": v(122.27, 73.06) * mm, "end": v(89.92, 75.84) * mm});
            skPoint(sketch, "E281.endSnap0", {"position": v(89.92, 75.87) * mm});
            skLineSegment(sketch, "E282", {"start": v(89.92, 75.84) * mm, "end": v(99.44, 97.3) * mm});
            skLineSegment(sketch, "E283", {"start": v(99.44, 97.3) * mm, "end": v(119.46, 93.1) * mm});
            skLineSegment(sketch, "E284", {"start": v(119.46, 93.1) * mm, "end": v(122.27, 73.06) * mm});
            skSolve(sketch);
        }
        {
            var Q0;
            Q0=qSketchRegion(id+"F4",true);
            var Q1;
            Q1=makeQuery(id+"F1.opExtrude","CAP_FACE",FACE,{"disambiguationData":[OSD([sQuery(id+"F0.wireOp",EDGE,"E0"),sQuery(id+"F0.wireOp",EDGE,"E1"),sQuery(id+"F0.wireOp",EDGE,"E2"),sQuery(id+"F0.wireOp",EDGE,"E3"),sQuery(id+"F0.wireOp",EDGE,"E4"),sQuery(id+"F0.wireOp",EDGE,"E5"),sQuery(id+"F0.wireOp",EDGE,"E6"),sQuery(id+"F0.wireOp",EDGE,"E7"),sQuery(id+"F0.wireOp",EDGE,"E8"),sQuery(id+"F0.wireOp",EDGE,"E9"),sQuery(id+"F0.wireOp",EDGE,"E10"),sQuery(id+"F0.wireOp",EDGE,"E11"),sQuery(id+"F0.wireOp",EDGE,"E12"),sQuery(id+"F0.wireOp",EDGE,"E13"),sQuery(id+"F0.wireOp",EDGE,"E14"),sQuery(id+"F0.wireOp",EDGE,"E15"),sQuery(id+"F0.wireOp",EDGE,"E16"),sQuery(id+"F0.wireOp",EDGE,"E17"),sQuery(id+"F0.wireOp",EDGE,"E18"),sQuery(id+"F0.wireOp",EDGE,"E19"),sQuery(id+"F0.wireOp",EDGE,"E20"),sQuery(id+"F0.wireOp",EDGE,"E21"),sQuery(id+"F0.wireOp",EDGE,"E22"),sQuery(id+"F0.wireOp",EDGE,"E23"),sQuery(id+"F0.wireOp",EDGE,"E24"),sQuery(id+"F0.wireOp",EDGE,"E25"),sQuery(id+"F0.wireOp",EDGE,"E26"),sQuery(id+"F0.wireOp",EDGE,"E27"),sQuery(id+"F0.wireOp",EDGE,"E28"),sQuery(id+"F0.wireOp",EDGE,"E29"),sQuery(id+"F0.wireOp",EDGE,"E30"),sQuery(id+"F0.wireOp",EDGE,"E31"),sQuery(id+"F0.wireOp",EDGE,"E32"),sQuery(id+"F0.wireOp",EDGE,"E33"),sQuery(id+"F0.wireOp",EDGE,"E34"),sQuery(id+"F0.wireOp",EDGE,"E35"),sQuery(id+"F0.wireOp",EDGE,"E36"),sQuery(id+"F0.wireOp",EDGE,"E37"),sQuery(id+"F0.wireOp",EDGE,"E38"),sQuery(id+"F0.wireOp",EDGE,"E39"),sQuery(id+"F0.wireOp",EDGE,"E40"),sQuery(id+"F0.wireOp",EDGE,"E41"),sQuery(id+"F0.wireOp",EDGE,"E42"),sQuery(id+"F0.wireOp",EDGE,"E43"),sQuery(id+"F0.wireOp",EDGE,"E44"),sQuery(id+"F0.wireOp",EDGE,"E45"),sQuery(id+"F0.wireOp",EDGE,"E46"),sQuery(id+"F0.wireOp",EDGE,"E47"),sQuery(id+"F0.wireOp",EDGE,"E48"),sQuery(id+"F0.wireOp",EDGE,"E49"),sQuery(id+"F0.wireOp",EDGE,"E50"),sQuery(id+"F0.wireOp",EDGE,"E51"),sQuery(id+"F0.wireOp",EDGE,"E52"),sQuery(id+"F0.wireOp",EDGE,"E53"),sQuery(id+"F0.wireOp",EDGE,"E54"),sQuery(id+"F0.wireOp",EDGE,"E55"),sQuery(id+"F0.wireOp",EDGE,"E56"),sQuery(id+"F0.wireOp",EDGE,"E57"),sQuery(id+"F0.wireOp",EDGE,"E58"),sQuery(id+"F0.wireOp",EDGE,"E59"),sQuery(id+"F0.wireOp",EDGE,"E60"),sQuery(id+"F0.wireOp",EDGE,"E61"),sQuery(id+"F0.wireOp",EDGE,"E62"),sQuery(id+"F0.wireOp",EDGE,"E63"),sQuery(id+"F0.wireOp",EDGE,"E64"),sQuery(id+"F0.wireOp",EDGE,"E65"),sQuery(id+"F0.wireOp",EDGE,"E66"),sQuery(id+"F0.wireOp",EDGE,"E67"),sQuery(id+"F0.wireOp",EDGE,"E68"),sQuery(id+"F0.wireOp",EDGE,"E69"),sQuery(id+"F0.wireOp",EDGE,"E70"),sQuery(id+"F0.wireOp",EDGE,"E71"),sQuery(id+"F0.wireOp",EDGE,"E72"),sQuery(id+"F0.wireOp",EDGE,"E73"),sQuery(id+"F0.wireOp",EDGE,"E74"),sQuery(id+"F0.wireOp",EDGE,"E75"),sQuery(id+"F0.wireOp",EDGE,"E76"),sQuery(id+"F0.wireOp",EDGE,"E77"),sQuery(id+"F0.wireOp",EDGE,"E78"),sQuery(id+"F0.wireOp",EDGE,"E79"),sQuery(id+"F0.wireOp",EDGE,"E80"),sQuery(id+"F0.wireOp",EDGE,"E81"),sQuery(id+"F0.wireOp",EDGE,"E82"),sQuery(id+"F0.wireOp",EDGE,"E83"),sQuery(id+"F0.wireOp",EDGE,"E84"),sQuery(id+"F0.wireOp",EDGE,"E85"),sQuery(id+"F0.wireOp",EDGE,"E86"),sQuery(id+"F0.wireOp",EDGE,"E87"),sQuery(id+"F0.wireOp",EDGE,"E88"),sQuery(id+"F0.wireOp",EDGE,"E89"),sQuery(id+"F0.wireOp",EDGE,"E90"),sQuery(id+"F0.wireOp",EDGE,"E91"),sQuery(id+"F0.wireOp",EDGE,"E92"),sQuery(id+"F0.wireOp",EDGE,"E93"),sQuery(id+"F0.wireOp",EDGE,"E94"),sQuery(id+"F0.wireOp",EDGE,"E95"),sQuery(id+"F0.wireOp",EDGE,"E96"),sQuery(id+"F0.wireOp",EDGE,"E97"),sQuery(id+"F0.wireOp",EDGE,"E98"),sQuery(id+"F0.wireOp",EDGE,"E99"),sQuery(id+"F0.wireOp",EDGE,"E100"),sQuery(id+"F0.wireOp",EDGE,"E101"),sQuery(id+"F0.wireOp",EDGE,"E102"),sQuery(id+"F0.wireOp",EDGE,"E103"),sQuery(id+"F0.wireOp",EDGE,"E104"),sQuery(id+"F0.wireOp",EDGE,"E105"),sQuery(id+"F0.wireOp",EDGE,"E106"),sQuery(id+"F0.wireOp",EDGE,"E107"),sQuery(id+"F0.wireOp",EDGE,"E108"),sQuery(id+"F0.wireOp",EDGE,"E109"),sQuery(id+"F0.wireOp",EDGE,"E110"),sQuery(id+"F0.wireOp",EDGE,"E111"),sQuery(id+"F0.wireOp",EDGE,"E112"),sQuery(id+"F0.wireOp",EDGE,"E113"),sQuery(id+"F0.wireOp",EDGE,"E114"),sQuery(id+"F0.wireOp",EDGE,"E115"),sQuery(id+"F0.wireOp",EDGE,"E116"),sQuery(id+"F0.wireOp",EDGE,"E117"),sQuery(id+"F0.wireOp",EDGE,"E118"),sQuery(id+"F0.wireOp",EDGE,"E119"),sQuery(id+"F0.wireOp",EDGE,"E120"),sQuery(id+"F0.wireOp",EDGE,"E121"),sQuery(id+"F0.wireOp",EDGE,"E122"),sQuery(id+"F0.wireOp",EDGE,"E123"),sQuery(id+"F0.wireOp",EDGE,"E124"),sQuery(id+"F0.wireOp",EDGE,"E125"),sQuery(id+"F0.wireOp",EDGE,"E126"),sQuery(id+"F0.wireOp",EDGE,"E127"),sQuery(id+"F0.wireOp",EDGE,"E128"),sQuery(id+"F0.wireOp",EDGE,"E129"),sQuery(id+"F0.wireOp",EDGE,"E130"),sQuery(id+"F0.wireOp",EDGE,"E131"),sQuery(id+"F0.wireOp",EDGE,"E132"),sQuery(id+"F0.wireOp",EDGE,"E133"),sQuery(id+"F0.wireOp",EDGE,"E134"),sQuery(id+"F0.wireOp",EDGE,"E135"),sQuery(id+"F0.wireOp",EDGE,"E136"),sQuery(id+"F0.wireOp",EDGE,"E137"),sQuery(id+"F0.wireOp",EDGE,"E138"),sQuery(id+"F0.wireOp",EDGE,"E139"),sQuery(id+"F0.wireOp",EDGE,"E140"),sQuery(id+"F0.wireOp",EDGE,"E141"),sQuery(id+"F0.wireOp",EDGE,"E142"),sQuery(id+"F0.wireOp",EDGE,"E143"),sQuery(id+"F0.wireOp",EDGE,"E144"),sQuery(id+"F0.wireOp",EDGE,"E145"),sQuery(id+"F0.wireOp",EDGE,"E146"),sQuery(id+"F0.wireOp",EDGE,"E147"),sQuery(id+"F0.wireOp",EDGE,"E148"),sQuery(id+"F0.wireOp",EDGE,"E149"),sQuery(id+"F0.wireOp",EDGE,"E150"),sQuery(id+"F0.wireOp",EDGE,"E151"),sQuery(id+"F0.wireOp",EDGE,"E152"),sQuery(id+"F0.wireOp",EDGE,"E153"),sQuery(id+"F0.wireOp",EDGE,"E154"),sQuery(id+"F0.wireOp",EDGE,"E155"),sQuery(id+"F0.wireOp",EDGE,"E156"),sQuery(id+"F0.wireOp",EDGE,"E157"),sQuery(id+"F0.wireOp",EDGE,"E158"),sQuery(id+"F0.wireOp",EDGE,"E159"),sQuery(id+"F0.wireOp",EDGE,"E160"),sQuery(id+"F0.wireOp",EDGE,"E161"),sQuery(id+"F0.wireOp",EDGE,"E162"),sQuery(id+"F0.wireOp",EDGE,"E163"),sQuery(id+"F0.wireOp",EDGE,"E164"),sQuery(id+"F0.wireOp",EDGE,"E165"),sQuery(id+"F0.wireOp",EDGE,"E166"),sQuery(id+"F0.wireOp",EDGE,"E167"),sQuery(id+"F0.wireOp",EDGE,"E168"),sQuery(id+"F0.wireOp",EDGE,"E169"),sQuery(id+"F0.wireOp",EDGE,"E170"),sQuery(id+"F0.wireOp",EDGE,"E171"),sQuery(id+"F0.wireOp",EDGE,"E172"),sQuery(id+"F0.wireOp",EDGE,"E173"),sQuery(id+"F0.wireOp",EDGE,"E174"),sQuery(id+"F0.wireOp",EDGE,"E175"),sQuery(id+"F0.wireOp",EDGE,"E176"),sQuery(id+"F0.wireOp",EDGE,"E177"),sQuery(id+"F0.wireOp",EDGE,"E178"),sQuery(id+"F0.wireOp",EDGE,"E179"),sQuery(id+"F0.wireOp",EDGE,"E180"),sQuery(id+"F0.wireOp",EDGE,"E181"),sQuery(id+"F0.wireOp",EDGE,"E182"),sQuery(id+"F0.wireOp",EDGE,"E183"),sQuery(id+"F0.wireOp",EDGE,"E184"),sQuery(id+"F0.wireOp",EDGE,"E185"),sQuery(id+"F0.wireOp",EDGE,"E186"),sQuery(id+"F0.wireOp",EDGE,"E187"),sQuery(id+"F0.wireOp",EDGE,"E188"),sQuery(id+"F0.wireOp",EDGE,"E189"),sQuery(id+"F0.wireOp",EDGE,"E190"),sQuery(id+"F0.wireOp",EDGE,"E191"),sQuery(id+"F0.wireOp",EDGE,"E192")])],"isStart":true});
            extrude(context, id + "F5", {"entities" : qUnion([Q0]), "operationType" : NewBodyOperationType.REMOVE, "endBound" : BoundingType.UP_TO_SURFACE, "oppositeDirection" : true, "endBoundEntityFace" : qUnion([Q1]), "depth" : 70.87 * mm});
        }
        {
            var Q0;
            Q0=makeQuery(id+"F5.boolean.opBoolean","SPLIT",BODY,{"disambiguationData":[OD(0.0)],"derivedFrom":makeQuery(id+"F3.opExtrude","SWEPT_BODY",BODY,{"disambiguationData":[OSD([sQuery(id+"F2.wireOp",EDGE,"E193"),sQuery(id+"F2.wireOp",EDGE,"E194"),sQuery(id+"F2.wireOp",EDGE,"E195"),sQuery(id+"F2.wireOp",EDGE,"E196"),sQuery(id+"F2.wireOp",EDGE,"E197"),sQuery(id+"F2.wireOp",EDGE,"E198"),sQuery(id+"F2.wireOp",EDGE,"E199"),sQuery(id+"F2.wireOp",EDGE,"E200"),sQuery(id+"F2.wireOp",EDGE,"E201"),sQuery(id+"F2.wireOp",EDGE,"E202"),sQuery(id+"F2.wireOp",EDGE,"E203"),sQuery(id+"F2.wireOp",EDGE,"E204"),sQuery(id+"F2.wireOp",EDGE,"E205"),sQuery(id+"F2.wireOp",EDGE,"E206"),sQuery(id+"F2.wireOp",EDGE,"E207"),sQuery(id+"F2.wireOp",EDGE,"E208"),sQuery(id+"F2.wireOp",EDGE,"E209"),sQuery(id+"F2.wireOp",EDGE,"E210"),sQuery(id+"F2.wireOp",EDGE,"E211"),sQuery(id+"F2.wireOp",EDGE,"E212"),sQuery(id+"F2.wireOp",EDGE,"E213"),sQuery(id+"F2.wireOp",EDGE,"E214"),sQuery(id+"F2.wireOp",EDGE,"E215"),sQuery(id+"F2.wireOp",EDGE,"E216"),sQuery(id+"F2.wireOp",EDGE,"E217"),sQuery(id+"F2.wireOp",EDGE,"E218"),sQuery(id+"F2.wireOp",EDGE,"E219"),sQuery(id+"F2.wireOp",EDGE,"E220"),sQuery(id+"F2.wireOp",EDGE,"E221"),sQuery(id+"F2.wireOp",EDGE,"E222"),sQuery(id+"F2.wireOp",EDGE,"E223"),sQuery(id+"F2.wireOp",EDGE,"E224"),sQuery(id+"F2.wireOp",EDGE,"E225"),sQuery(id+"F2.wireOp",EDGE,"E226"),sQuery(id+"F2.wireOp",EDGE,"E227"),sQuery(id+"F2.wireOp",EDGE,"E228"),sQuery(id+"F2.wireOp",EDGE,"E229"),sQuery(id+"F2.wireOp",EDGE,"E230"),sQuery(id+"F2.wireOp",EDGE,"E231"),sQuery(id+"F2.wireOp",EDGE,"E232"),sQuery(id+"F2.wireOp",EDGE,"E233"),sQuery(id+"F2.wireOp",EDGE,"E234"),sQuery(id+"F2.wireOp",EDGE,"E235"),sQuery(id+"F2.wireOp",EDGE,"E236"),sQuery(id+"F2.wireOp",EDGE,"E237"),sQuery(id+"F2.wireOp",EDGE,"E238"),sQuery(id+"F2.wireOp",EDGE,"E239"),sQuery(id+"F2.wireOp",EDGE,"E240"),sQuery(id+"F2.wireOp",EDGE,"E241"),sQuery(id+"F2.wireOp",EDGE,"E242"),sQuery(id+"F2.wireOp",EDGE,"E243"),sQuery(id+"F2.wireOp",EDGE,"E244"),sQuery(id+"F2.wireOp",EDGE,"E245"),sQuery(id+"F2.wireOp",EDGE,"E246"),sQuery(id+"F2.wireOp",EDGE,"E247"),sQuery(id+"F2.wireOp",EDGE,"E248"),sQuery(id+"F2.wireOp",EDGE,"E249"),sQuery(id+"F2.wireOp",EDGE,"E250"),sQuery(id+"F2.wireOp",EDGE,"E251"),sQuery(id+"F2.wireOp",EDGE,"E252"),sQuery(id+"F2.wireOp",EDGE,"E253"),sQuery(id+"F2.wireOp",EDGE,"E254"),sQuery(id+"F2.wireOp",EDGE,"E255"),sQuery(id+"F2.wireOp",EDGE,"E256"),sQuery(id+"F2.wireOp",EDGE,"E257"),sQuery(id+"F2.wireOp",EDGE,"E258"),sQuery(id+"F2.wireOp",EDGE,"E259"),sQuery(id+"F2.wireOp",EDGE,"E260"),sQuery(id+"F2.wireOp",EDGE,"E261"),sQuery(id+"F2.wireOp",EDGE,"E262"),sQuery(id+"F2.wireOp",EDGE,"E263"),sQuery(id+"F2.wireOp",EDGE,"E264"),sQuery(id+"F2.wireOp",EDGE,"E265"),sQuery(id+"F2.wireOp",EDGE,"E266"),sQuery(id+"F2.wireOp",EDGE,"E267"),sQuery(id+"F2.wireOp",EDGE,"E268"),sQuery(id+"F2.wireOp",EDGE,"E269"),sQuery(id+"F2.wireOp",EDGE,"E270"),sQuery(id+"F2.wireOp",EDGE,"E271"),sQuery(id+"F2.wireOp",EDGE,"E272"),sQuery(id+"F2.wireOp",EDGE,"E273"),sQuery(id+"F2.wireOp",EDGE,"E274"),sQuery(id+"F2.wireOp",EDGE,"E275"),sQuery(id+"F2.wireOp",EDGE,"E276"),sQuery(id+"F2.wireOp",EDGE,"E277"),sQuery(id+"F2.wireOp",EDGE,"E278"),sQuery(id+"F2.wireOp",EDGE,"E279"),sQuery(id+"F2.wireOp",EDGE,"E280")])]})});
            var Q1;
            Q1=makeQuery(id+"F3.opExtrude","CAP_EDGE",EDGE,{"disambiguationData":[OSD([sQuery(id+"F2.wireOp",EDGE,"E269")])],"isStart":false});
            var Q2;
            Q2=makeQuery(id+"F1.opExtrude","CAP_EDGE",EDGE,{"disambiguationData":[OSD([sQuery(id+"F0.wireOp",EDGE,"E161")])],"isStart":true});
            transform(context, id + "F6", {"entities" : qUnion([Q0]), "transformType" : TransformType.TRANSLATION_DISTANCE, "transformDirection" : qUnion([Q2]), "distance" : 52.83 * mm, "makeCopy" : false});
        }
        {
            var Q0;
            Q0=makeQuery(id+"F5.boolean.opBoolean","SPLIT",BODY,{"disambiguationData":[OD(0.0)],"derivedFrom":makeQuery(id+"F3.opExtrude","SWEPT_BODY",BODY,{"disambiguationData":[OSD([sQuery(id+"F2.wireOp",EDGE,"E193"),sQuery(id+"F2.wireOp",EDGE,"E194"),sQuery(id+"F2.wireOp",EDGE,"E195"),sQuery(id+"F2.wireOp",EDGE,"E196"),sQuery(id+"F2.wireOp",EDGE,"E197"),sQuery(id+"F2.wireOp",EDGE,"E198"),sQuery(id+"F2.wireOp",EDGE,"E199"),sQuery(id+"F2.wireOp",EDGE,"E200"),sQuery(id+"F2.wireOp",EDGE,"E201"),sQuery(id+"F2.wireOp",EDGE,"E202"),sQuery(id+"F2.wireOp",EDGE,"E203"),sQuery(id+"F2.wireOp",EDGE,"E204"),sQuery(id+"F2.wireOp",EDGE,"E205"),sQuery(id+"F2.wireOp",EDGE,"E206"),sQuery(id+"F2.wireOp",EDGE,"E207"),sQuery(id+"F2.wireOp",EDGE,"E208"),sQuery(id+"F2.wireOp",EDGE,"E209"),sQuery(id+"F2.wireOp",EDGE,"E210"),sQuery(id+"F2.wireOp",EDGE,"E211"),sQuery(id+"F2.wireOp",EDGE,"E212"),sQuery(id+"F2.wireOp",EDGE,"E213"),sQuery(id+"F2.wireOp",EDGE,"E214"),sQuery(id+"F2.wireOp",EDGE,"E215"),sQuery(id+"F2.wireOp",EDGE,"E216"),sQuery(id+"F2.wireOp",EDGE,"E217"),sQuery(id+"F2.wireOp",EDGE,"E218"),sQuery(id+"F2.wireOp",EDGE,"E219"),sQuery(id+"F2.wireOp",EDGE,"E220"),sQuery(id+"F2.wireOp",EDGE,"E221"),sQuery(id+"F2.wireOp",EDGE,"E222"),sQuery(id+"F2.wireOp",EDGE,"E223"),sQuery(id+"F2.wireOp",EDGE,"E224"),sQuery(id+"F2.wireOp",EDGE,"E225"),sQuery(id+"F2.wireOp",EDGE,"E226"),sQuery(id+"F2.wireOp",EDGE,"E227"),sQuery(id+"F2.wireOp",EDGE,"E228"),sQuery(id+"F2.wireOp",EDGE,"E229"),sQuery(id+"F2.wireOp",EDGE,"E230"),sQuery(id+"F2.wireOp",EDGE,"E231"),sQuery(id+"F2.wireOp",EDGE,"E232"),sQuery(id+"F2.wireOp",EDGE,"E233"),sQuery(id+"F2.wireOp",EDGE,"E234"),sQuery(id+"F2.wireOp",EDGE,"E235"),sQuery(id+"F2.wireOp",EDGE,"E236"),sQuery(id+"F2.wireOp",EDGE,"E237"),sQuery(id+"F2.wireOp",EDGE,"E238"),sQuery(id+"F2.wireOp",EDGE,"E239"),sQuery(id+"F2.wireOp",EDGE,"E240"),sQuery(id+"F2.wireOp",EDGE,"E241"),sQuery(id+"F2.wireOp",EDGE,"E242"),sQuery(id+"F2.wireOp",EDGE,"E243"),sQuery(id+"F2.wireOp",EDGE,"E244"),sQuery(id+"F2.wireOp",EDGE,"E245"),sQuery(id+"F2.wireOp",EDGE,"E246"),sQuery(id+"F2.wireOp",EDGE,"E247"),sQuery(id+"F2.wireOp",EDGE,"E248"),sQuery(id+"F2.wireOp",EDGE,"E249"),sQuery(id+"F2.wireOp",EDGE,"E250"),sQuery(id+"F2.wireOp",EDGE,"E251"),sQuery(id+"F2.wireOp",EDGE,"E252"),sQuery(id+"F2.wireOp",EDGE,"E253"),sQuery(id+"F2.wireOp",EDGE,"E254"),sQuery(id+"F2.wireOp",EDGE,"E255"),sQuery(id+"F2.wireOp",EDGE,"E256"),sQuery(id+"F2.wireOp",EDGE,"E257"),sQuery(id+"F2.wireOp",EDGE,"E258"),sQuery(id+"F2.wireOp",EDGE,"E259"),sQuery(id+"F2.wireOp",EDGE,"E260"),sQuery(id+"F2.wireOp",EDGE,"E261"),sQuery(id+"F2.wireOp",EDGE,"E262"),sQuery(id+"F2.wireOp",EDGE,"E263"),sQuery(id+"F2.wireOp",EDGE,"E264"),sQuery(id+"F2.wireOp",EDGE,"E265"),sQuery(id+"F2.wireOp",EDGE,"E266"),sQuery(id+"F2.wireOp",EDGE,"E267"),sQuery(id+"F2.wireOp",EDGE,"E268"),sQuery(id+"F2.wireOp",EDGE,"E269"),sQuery(id+"F2.wireOp",EDGE,"E270"),sQuery(id+"F2.wireOp",EDGE,"E271"),sQuery(id+"F2.wireOp",EDGE,"E272"),sQuery(id+"F2.wireOp",EDGE,"E273"),sQuery(id+"F2.wireOp",EDGE,"E274"),sQuery(id+"F2.wireOp",EDGE,"E275"),sQuery(id+"F2.wireOp",EDGE,"E276"),sQuery(id+"F2.wireOp",EDGE,"E277"),sQuery(id+"F2.wireOp",EDGE,"E278"),sQuery(id+"F2.wireOp",EDGE,"E279"),sQuery(id+"F2.wireOp",EDGE,"E280")])]})});
            var Q1;
            Q1=makeQuery(id+"F1.opExtrude","CAP_EDGE",EDGE,{"disambiguationData":[OSD([sQuery(id+"F0.wireOp",EDGE,"E168")])],"isStart":true});
            transform(context, id + "F7", {"entities" : qUnion([Q0]), "transformType" : TransformType.TRANSLATION_DISTANCE, "transformDirection" : qUnion([Q1]), "distance" : 37.34 * mm, "oppositeDirection" : true, "makeCopy" : false});
        }
    });
